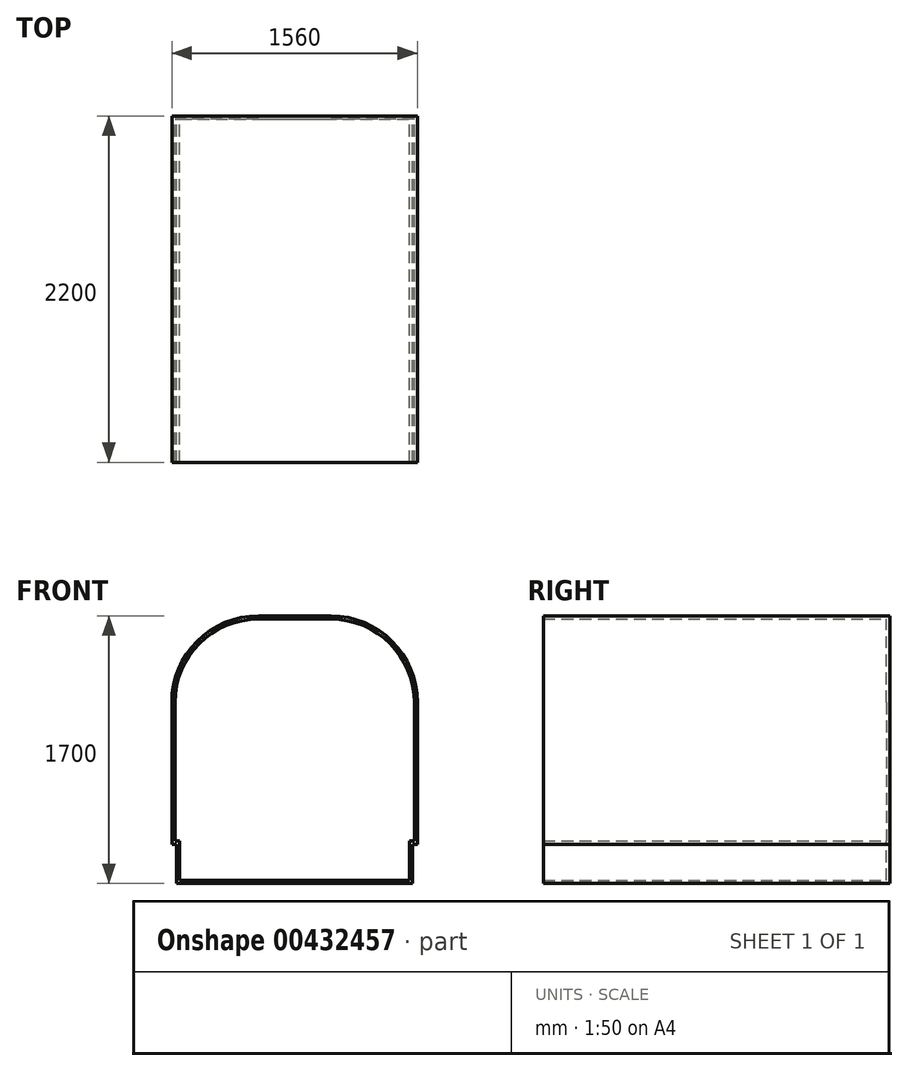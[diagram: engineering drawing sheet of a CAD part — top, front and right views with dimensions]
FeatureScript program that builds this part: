
annotation { "Feature Type Name" : "Feature", "Feature Type Description" : "" }
export const myFeature = defineFeature(function(context is Context, id is Id, definition is map)
    precondition{}
    {
        {
            var Q0;
            Q0=qCreatedBy(makeId("Front.planeOp"),FACE);
            var sketch = newSketch(context, id + "F0", { "sketchPlane" : qUnion([Q0])});
            skLineSegment(sketch, "E0", {"start": v(-750, 0) * mm, "end": v(750, 0) * mm});
            skLineSegment(sketch, "E1", {"start": v(-750, 0) * mm, "end": v(-750, 400) * mm});
            skLineSegment(sketch, "E2", {"start": v(750, 0) * mm, "end": v(750, 400) * mm});
            skLineSegment(sketch, "E3", {"start": v(-750, 400) * mm, "end": v(750, 400) * mm, "construction": true});
            skLineSegment(sketch, "E4", {"start": v(-230, 1700) * mm, "end": v(230, 1700) * mm});
            skLineSegment(sketch, "E5", {"start": v(0, 0) * mm, "end": v(0, 1700) * mm, "construction": true});
            skLineSegment(sketch, "E6", {"start": v(-1650, 400) * mm, "end": v(-450, 400) * mm, "construction": true});
            skLineSegment(sketch, "E7", {"start": v(-780, 1150) * mm, "end": v(-780, 250) * mm});
            skLineSegment(sketch, "E8.MirrorCS", {"start": v(780, 1150) * mm, "end": v(780, 250) * mm});
            skLineSegment(sketch, "E9", {"start": v(-780, 1150) * mm, "end": v(-780, 1150) * mm});
            skLineSegment(sketch, "E10", {"start": v(780, 1150) * mm, "end": v(780, 1150) * mm});
            skPoint(sketch, "E11.visualSharp", {"position": v(-600, 1700) * mm});
            skArc(sketch, "E11.filletArc", {"start": v(-230, 1700) * mm, "mid": v(-618.9, 1538.9) * mm, "end": v(-780, 1150) * mm});
            skPoint(sketch, "E12.visualSharp", {"position": v(600, 1700) * mm});
            skArc(sketch, "E12.filletArc", {"start": v(780, 1150) * mm, "mid": v(618.9, 1538.9) * mm, "end": v(230, 1700) * mm});
            skLineSegment(sketch, "E13", {"start": v(-780, 250) * mm, "end": v(-750, 250) * mm});
            skLineSegment(sketch, "E14", {"start": v(780, 250) * mm, "end": v(750, 250) * mm});
            skCircle(sketch, "E15", {"center": v(-746.35, 1339.43) * mm, "radius": 1089.95 * mm, "construction": true});
            skLineSegment(sketch, "E16", {"start": v(-1650, 400) * mm, "end": v(-1650, 730) * mm});
            skSolve(sketch);
        }
        {
            var Q0;
            Q0=qSketchRegion(id+"F0",true);
            extrude(context, id + "F1", {"entities" : qUnion([Q0]), "depth" : 2200 * mm});
        }
        {
            var Q0;
            Q0=makeQuery(id+"F1.opExtrude","CAP_FACE",FACE,{"disambiguationData":[OSD([sQuery(id+"F0.wireOp",EDGE,"E0"),sQuery(id+"F0.wireOp",EDGE,"E1"),sQuery(id+"F0.wireOp",EDGE,"E2"),sQuery(id+"F0.wireOp",EDGE,"E4"),sQuery(id+"F0.wireOp",EDGE,"3df741bf-00aa-4e76-a0c7-f7b0b77aa621"),sQuery(id+"F0.wireOp",EDGE,"6fed6d78-777c-4dff-9b01-a5f90d519f82"),sQuery(id+"F0.wireOp",EDGE,"bca19fb2-4df8-4f06-bd02-8d9c50e149b9"),sQuery(id+"F0.wireOp",EDGE,"E7"),sQuery(id+"F0.wireOp",EDGE,"c597f7f8-ba4b-4117-8ee7-06938dc063410.MirrorCS"),sQuery(id+"F0.wireOp",EDGE,"E8.MirrorCS"),sQuery(id+"F0.wireOp",EDGE,"3b7a2c63-392d-4415-9d25-b7fee838797f"),sQuery(id+"F0.wireOp",EDGE,"1df09146-72df-46f6-88e9-4f3c2d156cca")])],"isStart":false});
            shell(context, id + "F2", {"entities" : qUnion([Q0]), "thickness" : 20 * mm});
        }
    });
